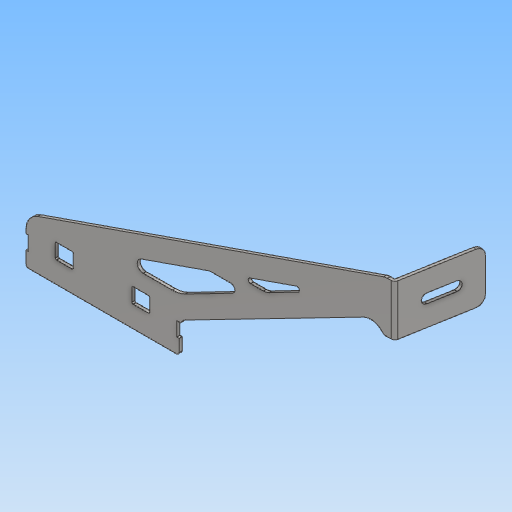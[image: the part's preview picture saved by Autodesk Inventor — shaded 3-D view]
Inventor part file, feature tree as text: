
AUTODESK INVENTOR PART (.ipt)
format: ipt  version: 2020 (Build 240168000, 168)  size: 472,576 bytes
history: native  units: mm
features: other x3, extrude x1, plane x1
ambient origin geometry x8: Origin, YZ Plane, XZ Plane, XY Plane, X Axis, Y Axis, Z Axis, Center Point
bodies: Body1 (feature_tree)
feature tree (5):
  other  "實體1"
  extrude  "擠出1"  Depth=130.0mm
  other  "折彎零件1"
  plane  "工作平面1"
  other  "定義1"
